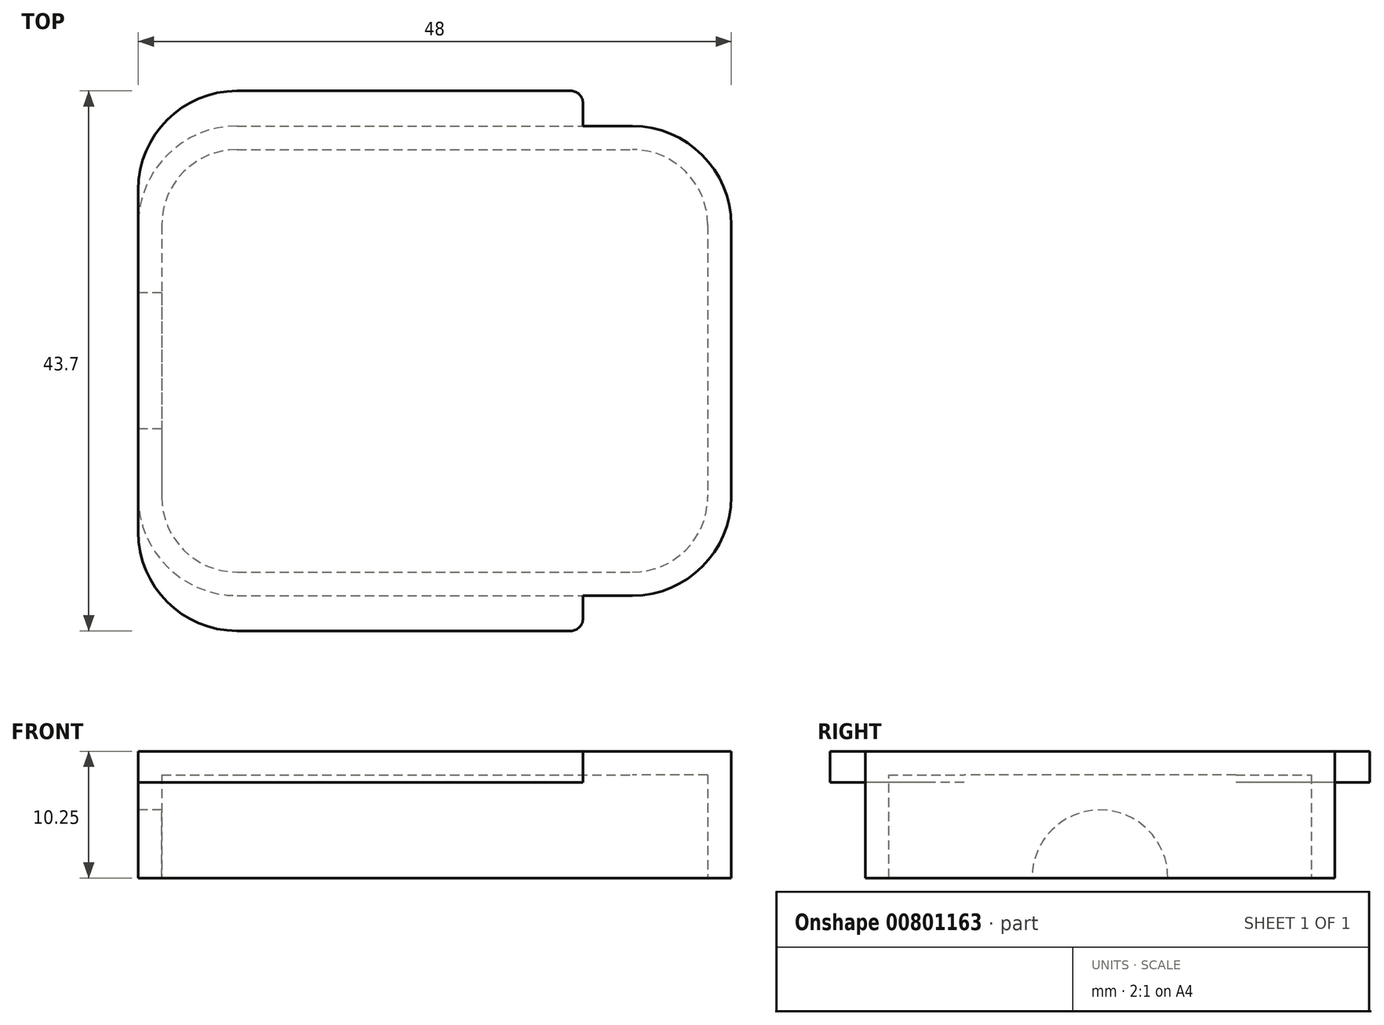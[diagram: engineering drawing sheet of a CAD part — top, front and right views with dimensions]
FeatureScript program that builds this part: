
annotation { "Feature Type Name" : "Feature", "Feature Type Description" : "" }
export const myFeature = defineFeature(function(context is Context, id is Id, definition is map)
    precondition{}
    {
        {
            var Q0;
            Q0=qCreatedBy(makeId("Top.planeOp"),FACE);
            var sketch = newSketch(context, id + "F0", { "sketchPlane" : qUnion([Q0])});
            skLineSegment(sketch, "E0.bottom", {"start": v(-16, 19) * mm, "end": v(16, 19) * mm});
            skLineSegment(sketch, "E0.top", {"start": v(-16, -19) * mm, "end": v(16, -19) * mm});
            skLineSegment(sketch, "E0.left", {"start": v(-24, 11) * mm, "end": v(-24, -11) * mm});
            skLineSegment(sketch, "E0.right", {"start": v(24, 11) * mm, "end": v(24, -11) * mm});
            skPoint(sketch, "E1.visualSharp", {"position": v(-24, 19) * mm});
            skArc(sketch, "E1.filletArc", {"start": v(-16, 19) * mm, "mid": v(-21.66, 16.66) * mm, "end": v(-24, 11) * mm});
            skPoint(sketch, "E2.visualSharp", {"position": v(24, 19) * mm});
            skArc(sketch, "E2.filletArc", {"start": v(24, 11) * mm, "mid": v(21.66, 16.66) * mm, "end": v(16, 19) * mm});
            skPoint(sketch, "E3.visualSharp", {"position": v(24, -19) * mm});
            skArc(sketch, "E3.filletArc", {"start": v(16, -19) * mm, "mid": v(21.66, -16.66) * mm, "end": v(24, -11) * mm});
            skPoint(sketch, "E4.visualSharp", {"position": v(-24, -19) * mm});
            skArc(sketch, "E4.filletArc", {"start": v(-24, -11) * mm, "mid": v(-21.66, -16.66) * mm, "end": v(-16, -19) * mm});
            skSolve(sketch);
        }
        {
            var Q0;
            Q0=makeQuery(id+"F0.imprint","IMPRINT",FACE,{"disambiguationData":[TD([[makeQuery(id+"F0.imprint","IMPRINT",EDGE,{"derivedFrom":sQuery(id+"F0.wireOp",EDGE,"E0.bottom")}),-1.0]])]});
            extrude(context, id + "F1", {"entities" : qUnion([Q0]), "depth" : 10.25 * mm, "offsetDistance" : 25 * mm});
        }
        {
            var Q0;
            Q0=makeQuery(id+"F1.opExtrude","CAP_FACE",FACE,{"disambiguationData":[OSD([sQuery(id+"F0.wireOp",EDGE,"E0.bottom"),sQuery(id+"F0.wireOp",EDGE,"E0.top"),sQuery(id+"F0.wireOp",EDGE,"E0.left"),sQuery(id+"F0.wireOp",EDGE,"E0.right"),sQuery(id+"F0.wireOp",EDGE,"E1.filletArc"),sQuery(id+"F0.wireOp",EDGE,"E2.filletArc"),sQuery(id+"F0.wireOp",EDGE,"E3.filletArc"),sQuery(id+"F0.wireOp",EDGE,"E4.filletArc")])],"isStart":false});
            var sketch = newSketch(context, id + "F2", { "sketchPlane" : qUnion([Q0])});
            skLineSegment(sketch, "E5.bottom", {"start": v(-16, 21.85) * mm, "end": v(12, 21.85) * mm});
            skLineSegment(sketch, "E5.top", {"start": v(-16, -21.85) * mm, "end": v(12, -21.85) * mm});
            skLineSegment(sketch, "E5.left", {"start": v(-24, 13.85) * mm, "end": v(-24, -13.85) * mm});
            skLineSegment(sketch, "E5.right", {"start": v(12, 21.85) * mm, "end": v(12, -21.85) * mm});
            skPoint(sketch, "E6.visualSharp", {"position": v(-24, 21.85) * mm});
            skArc(sketch, "E6.filletArc", {"start": v(-16, 21.85) * mm, "mid": v(-21.66, 19.5) * mm, "end": v(-24, 13.85) * mm});
            skPoint(sketch, "E7.visualSharp", {"position": v(-24, -21.85) * mm});
            skArc(sketch, "E7.filletArc", {"start": v(-24, -13.85) * mm, "mid": v(-21.66, -19.5) * mm, "end": v(-16, -21.85) * mm});
            skSolve(sketch);
        }
        {
            var Q0;
            {var subQ4=sQuery(id+"F2.wireOp",EDGE,"E5.bottom");Q0=makeQuery(id+"F2.imprint","IMPRINT",FACE,{"disambiguationData":[TD([[makeQuery(id+"F2.imprint","IMPRINT",EDGE,{"derivedFrom":subQ4}),-1.0]])]});}
            var Q1;
            {var subQ1=sQuery(id+"F2.wireOp",EDGE,"E5.top");Q1=makeQuery(id+"F2.imprint","IMPRINT",FACE,{"disambiguationData":[TD([[makeQuery(id+"F2.imprint","IMPRINT",EDGE,{"derivedFrom":subQ1}),1.0]])]});}
            extrude(context, id + "F3", {"entities" : qUnion([Q0, Q1]), "operationType" : NewBodyOperationType.ADD, "oppositeDirection" : true, "depth" : 2.5 * mm, "offsetDistance" : 25 * mm});
        }
        {
            var Q0;
            Q0=makeQuery(id+"F3.opExtrude","SWEPT_EDGE",EDGE,{"disambiguationData":[OSD([sQuery(id+"F2.wireOp",EDGE,"E5.top"),sQuery(id+"F2.wireOp",EDGE,"E5.right")])]});
            var Q1;
            Q1=makeQuery(id+"F3.opExtrude","SWEPT_EDGE",EDGE,{"disambiguationData":[OSD([sQuery(id+"F0.wireOp",EDGE,"E0.top"),sQuery(id+"F2.wireOp",EDGE,"E5.right")])]});
            var Q2;
            Q2=makeQuery(id+"F3.opExtrude","SWEPT_EDGE",EDGE,{"disambiguationData":[OSD([sQuery(id+"F0.wireOp",EDGE,"E0.bottom"),sQuery(id+"F2.wireOp",EDGE,"E5.right")])]});
            var Q3;
            Q3=makeQuery(id+"F3.opExtrude","SWEPT_EDGE",EDGE,{"disambiguationData":[OSD([sQuery(id+"F2.wireOp",EDGE,"E5.bottom"),sQuery(id+"F2.wireOp",EDGE,"E5.right")])]});
            fillet(context, id + "F4", {"entities" : qUnion([Q0, Q1, Q2, Q3]), "radius" : 1 * mm, "tangentPropagation" : true, "allowEdgeOverflow" : false});
        }
        {
            var Q0;
            Q0=makeQuery(id+"F1.opExtrude","CAP_FACE",FACE,{"disambiguationData":[OSD([sQuery(id+"F0.wireOp",EDGE,"E0.bottom"),sQuery(id+"F0.wireOp",EDGE,"E0.top"),sQuery(id+"F0.wireOp",EDGE,"E0.left"),sQuery(id+"F0.wireOp",EDGE,"E0.right"),sQuery(id+"F0.wireOp",EDGE,"E1.filletArc"),sQuery(id+"F0.wireOp",EDGE,"E2.filletArc"),sQuery(id+"F0.wireOp",EDGE,"E3.filletArc"),sQuery(id+"F0.wireOp",EDGE,"E4.filletArc")])],"isStart":true});
            shell(context, id + "F5", {"entities" : qUnion([Q0]), "thickness" : 1.9 * mm});
        }
        {
            var Q0;
            {var subQ0=sQuery(id+"F2.wireOp",EDGE,"E5.left");Q0=makeQuery(id+"F3.boolean.opBoolean","MERGE",FACE,{"derivedFrom":[makeQuery(id+"F1.opExtrude","SWEPT_FACE",FACE,{"disambiguationData":[OSD([sQuery(id+"F0.wireOp",EDGE,"E0.left")])]}),makeQuery(id+"F3.opExtrude","SWEPT_FACE",FACE,{"disambiguationData":[OSD([subQ0]),TDD([makeQuery(id+"F2.imprint","IMPRINT",EDGE,{"disambiguationData":[TD([[makeQuery(id+"F2.imprint","INTERSECT",VERTEX,{"derivedFrom":[makeQuery(id+"F1.opExtrude","CAP_EDGE",EDGE,{"disambiguationData":[OSD([sQuery(id+"F0.wireOp",EDGE,"E1.filletArc")])],"isStart":false}),subQ0]}),1.0]])],"derivedFrom":subQ0})])]}),makeQuery(id+"F3.opExtrude","SWEPT_FACE",FACE,{"disambiguationData":[OSD([subQ0]),TDD([makeQuery(id+"F2.imprint","IMPRINT",EDGE,{"disambiguationData":[TD([[makeQuery(id+"F2.imprint","INTERSECT",VERTEX,{"derivedFrom":[makeQuery(id+"F1.opExtrude","CAP_EDGE",EDGE,{"disambiguationData":[OSD([sQuery(id+"F0.wireOp",EDGE,"E4.filletArc")])],"isStart":false}),subQ0]}),-1.0]])],"derivedFrom":subQ0})])]})]});}
            var sketch = newSketch(context, id + "F6", { "sketchPlane" : qUnion([Q0])});
            skPoint(sketch, "E8", {"position": v(0, 0) * mm});
            skCircle(sketch, "E9", {"center": v(0, 0) * mm, "radius": 5.5 * mm});
            skSolve(sketch);
        }
        {
            var Q0;
            Q0 = qSketchRegion(id + "F6", true);
            extrude(context, id + "F7", {"entities" : qUnion([Q0]), "operationType" : NewBodyOperationType.REMOVE, "oppositeDirection" : true, "depth" : 2 * mm, "offsetDistance" : 25 * mm});
        }
    });
